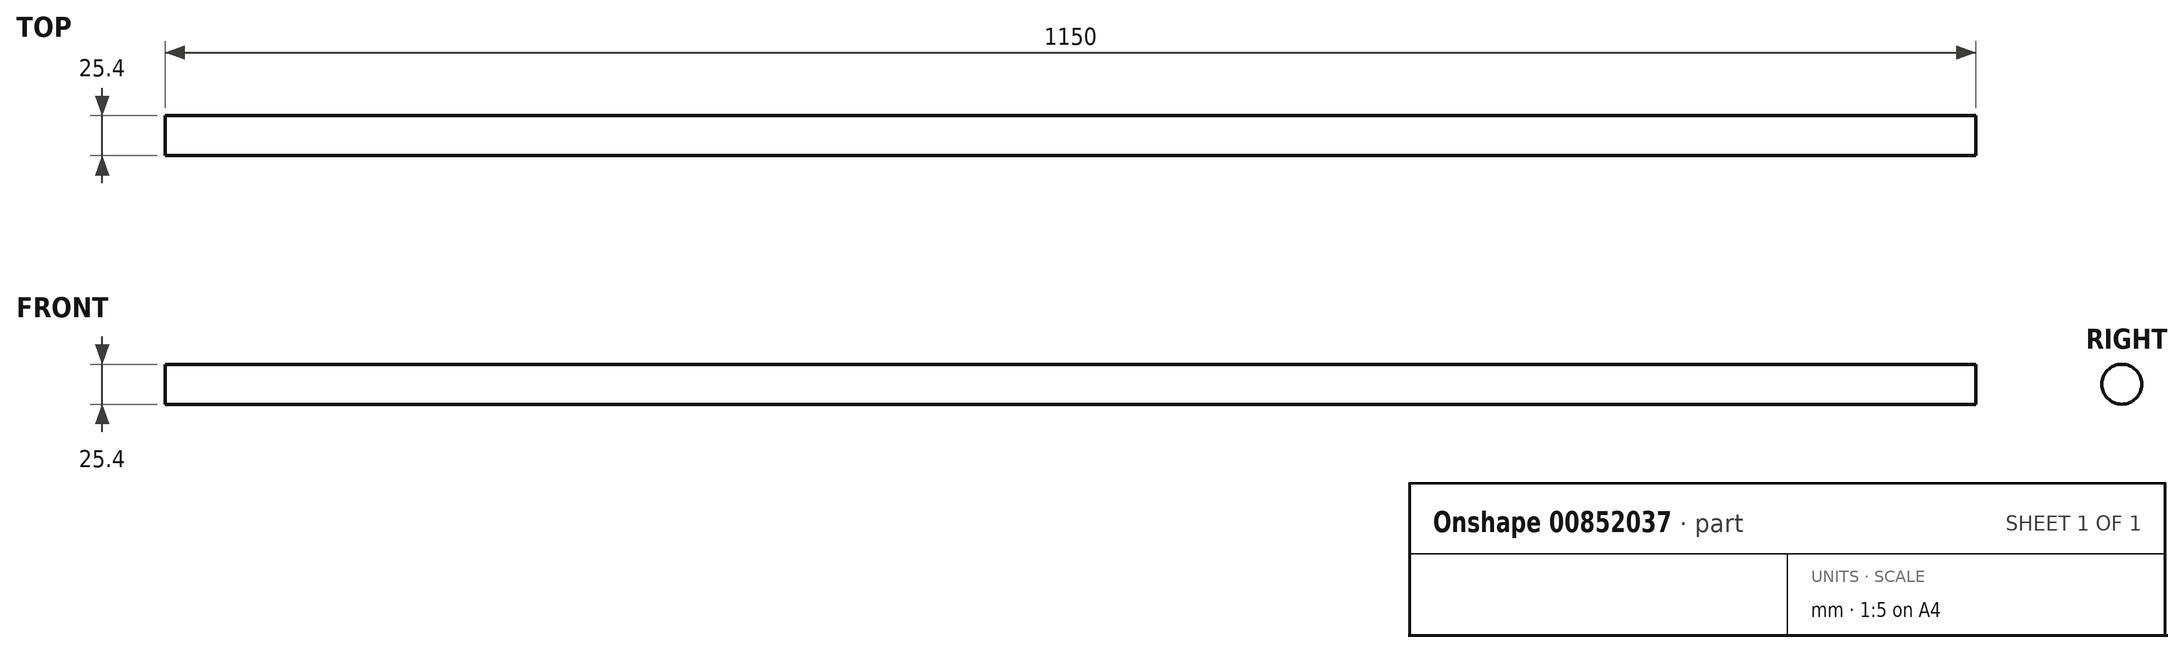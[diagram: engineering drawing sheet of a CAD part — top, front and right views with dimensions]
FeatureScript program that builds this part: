
annotation { "Feature Type Name" : "Feature", "Feature Type Description" : "" }
export const myFeature = defineFeature(function(context is Context, id is Id, definition is map)
    precondition{}
    {
        {
            var Q0;
            Q0=qCreatedBy(makeId("Right.planeOp"),FACE);
            var sketch = newSketch(context, id + "F0", { "sketchPlane" : qUnion([Q0])});
            skCircle(sketch, "E0", {"center": v(0, 0) * mm, "radius": 12.7 * mm});
            skSolve(sketch);
        }
        {
            var Q0;
            Q0=sQuery(id+"F0.wireOp",EDGE,"E0");
            extrude(context, id + "F1", {"bodyType" : ToolBodyType.SURFACE, "surfaceEntities" : qUnion([Q0]), "depth" : 1150 * mm, "offsetDistance" : 25.4 * mm});
        }
    });
